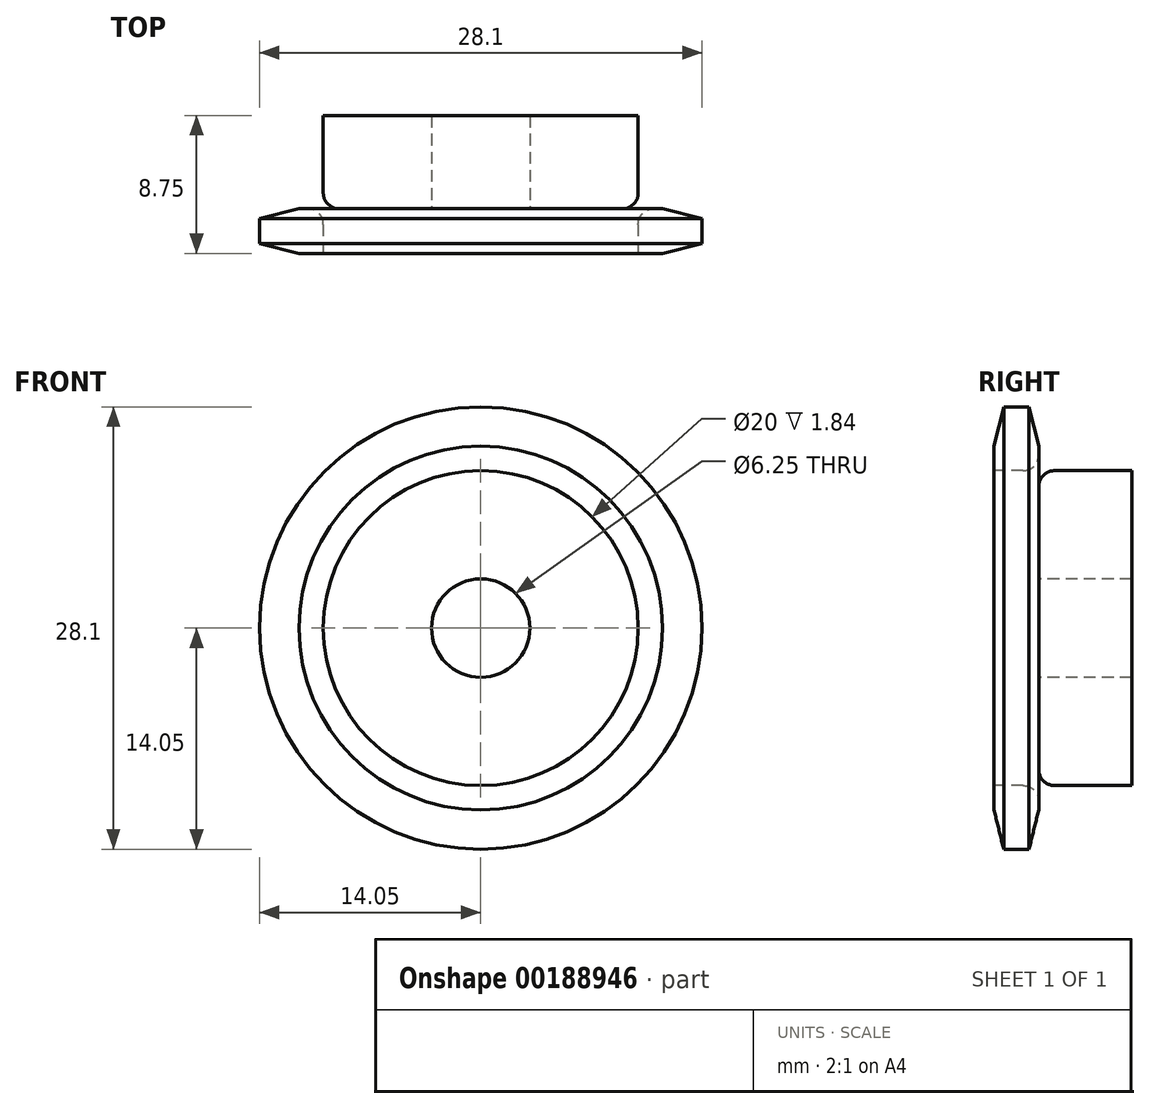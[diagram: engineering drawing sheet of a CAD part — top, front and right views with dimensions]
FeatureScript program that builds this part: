
annotation { "Feature Type Name" : "Feature", "Feature Type Description" : "" }
export const myFeature = defineFeature(function(context is Context, id is Id, definition is map)
    precondition{}
    {
        {
            var Q0;
            Q0=qCreatedBy(makeId("Right.planeOp"),FACE);
            var sketch = newSketch(context, id + "F0", { "sketchPlane" : qUnion([Q0])});
            skLineSegment(sketch, "E0", {"start": v(0, 0) * mm, "end": v(8.75, 0) * mm, "construction": true});
            skLineSegment(sketch, "E1.bottom", {"start": v(0, 3.12) * mm, "end": v(2.84, 3.12) * mm});
            skLineSegment(sketch, "E1.top", {"start": v(0, 14.05) * mm, "end": v(2.84, 14.05) * mm});
            skLineSegment(sketch, "E1.left", {"start": v(0, 3.12) * mm, "end": v(0, 14.05) * mm});
            skLineSegment(sketch, "E1.right", {"start": v(2.84, 3.12) * mm, "end": v(2.84, 14.05) * mm});
            skLineSegment(sketch, "E2.bottom", {"start": v(0, 3.12) * mm, "end": v(8.75, 3.12) * mm});
            skLineSegment(sketch, "E2.top", {"start": v(0, 10) * mm, "end": v(8.75, 10) * mm});
            skLineSegment(sketch, "E2.left", {"start": v(0, 3.12) * mm, "end": v(0, 10) * mm});
            skLineSegment(sketch, "E2.right", {"start": v(8.75, 3.12) * mm, "end": v(8.75, 10) * mm});
            skLineSegment(sketch, "E3.MirrorCS", {"start": v(0, -3.12) * mm, "end": v(2.84, -3.12) * mm});
            skLineSegment(sketch, "E4.MirrorCS", {"start": v(0, -3.12) * mm, "end": v(0, -10) * mm});
            skLineSegment(sketch, "E5.MirrorCS", {"start": v(0, -3.12) * mm, "end": v(8.75, -3.12) * mm});
            skLineSegment(sketch, "E6.MirrorCS", {"start": v(0, -3.12) * mm, "end": v(0, -14.05) * mm});
            skLineSegment(sketch, "E7.MirrorCS", {"start": v(0, -14.05) * mm, "end": v(2.84, -14.05) * mm});
            skLineSegment(sketch, "E8.MirrorCS", {"start": v(0, -10) * mm, "end": v(8.75, -10) * mm});
            skLineSegment(sketch, "E9.MirrorCS", {"start": v(2.84, -3.12) * mm, "end": v(2.84, -14.05) * mm});
            skLineSegment(sketch, "E10.MirrorCS", {"start": v(8.75, -3.12) * mm, "end": v(8.75, -10) * mm});
            skSolve(sketch);
        }
        {
            var Q0;
            {var subQ5=sQuery(id+"F0.wireOp",EDGE,"E2.right");Q0=makeQuery(id+"F0.imprint","IMPRINT",FACE,{"disambiguationData":[TD([[makeQuery(id+"F0.imprint","IMPRINT",EDGE,{"derivedFrom":subQ5}),1.0]])]});}
            var Q1;
            {var subQ5=sQuery(id+"F0.wireOp",EDGE,"E2.left");Q1=makeQuery(id+"F0.imprint","IMPRINT",FACE,{"disambiguationData":[TD([[makeQuery(id+"F0.imprint","IMPRINT",EDGE,{"derivedFrom":subQ5}),-1.0]])]});}
            var Q2;
            {var subQ0=sQuery(id+"F0.wireOp",EDGE,"E1.top");Q2=makeQuery(id+"F0.imprint","IMPRINT",FACE,{"disambiguationData":[TD([[makeQuery(id+"F0.imprint","IMPRINT",EDGE,{"derivedFrom":subQ0}),-1.0]])]});}
            var Q3;
            Q3=sQuery(id+"F0.wireOp",EDGE,"E0");
            revolve(context, id + "F1", {"entities" : qUnion([Q0, Q1, Q2]), "axis" : qUnion([Q3]), "revolveType" : RevolveType.FULL});
        }
        {
            var Q0;
            Q0=makeQuery(id+"F1.opRevolve","SWEPT_EDGE",EDGE,{"disambiguationData":[OSD([sQuery(id+"F0.wireOp",EDGE,"E1.right"),sQuery(id+"F0.wireOp",EDGE,"E2.top")])]});
            fillet(context, id + "F2", {"entities" : qUnion([Q0]), "radius" : 1 * mm, "tangentPropagation" : true, "allowEdgeOverflow" : false});
        }
        {
            var Q0;
            Q0=makeQuery(id+"F1.opRevolve","SWEPT_EDGE",EDGE,{"disambiguationData":[OSD([sQuery(id+"F0.wireOp",EDGE,"E1.top"),sQuery(id+"F0.wireOp",EDGE,"E1.left")])]});
            var Q1;
            Q1=makeQuery(id+"F1.opRevolve","SWEPT_EDGE",EDGE,{"disambiguationData":[OSD([sQuery(id+"F0.wireOp",EDGE,"E1.top"),sQuery(id+"F0.wireOp",EDGE,"E1.right")])]});
            chamfer(context, id + "F3", {"entities" : qUnion([Q0, Q1]), "chamferType" : ChamferType.TWO_OFFSETS, "width1" : 2.5 * mm, "oppositeDirection" : false, "width2" : 0.62 * mm, "tangentPropagation" : true});
        }
    });
